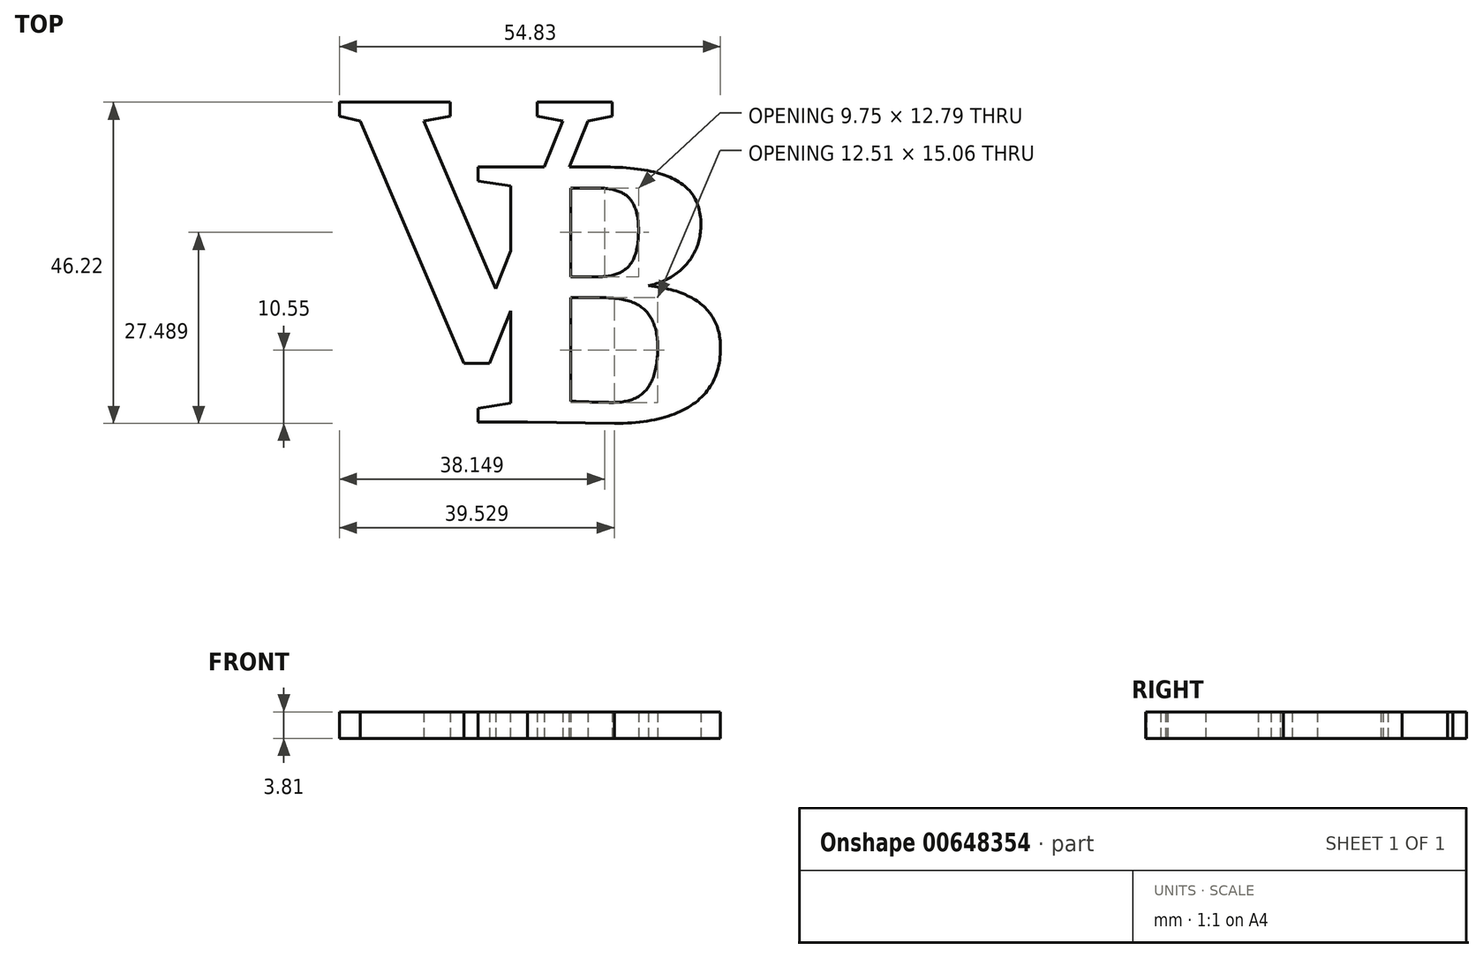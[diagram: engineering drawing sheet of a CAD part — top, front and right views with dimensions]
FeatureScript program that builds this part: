
annotation { "Feature Type Name" : "Feature", "Feature Type Description" : "" }
export const myFeature = defineFeature(function(context is Context, id is Id, definition is map)
    precondition{}
    {
        {
            var Q0;
            Q0=qCreatedBy(makeId("Top.planeOp"),FACE);
            var sketch = newSketch(context, id + "F0", { "sketchPlane" : qUnion([Q0])});
            skText(sketch, "E0", { "text": "V", "fontName": "Tinos-Bold.ttf"});
            const initialGuessF0  = {"E0": [-0.02997, -0.0202, 1, 0, 0.04038]};
            skSetInitialGuess(sketch, initialGuessF0);
            skSolve(sketch);
        }
        {
            var Q0;
            Q0 = qSketchRegion(id + "F0", true);
            extrude(context, id + "F1", {"entities" : qUnion([Q0]), "depth" : 3.8 * mm, "offsetDistance" : 25.4 * mm});
        }
        {
            var Q0;
            Q0=qCreatedBy(makeId("Top.planeOp"),FACE);
            var sketch = newSketch(context, id + "F2", { "sketchPlane" : qUnion([Q0])});
            skText(sketch, "E1", { "text": "B", "fontName": "Tinos-Bold.ttf"});
            const initialGuessF2  = {"E1": [-0.01036, -0.02952, 1, 0, 0.04038]};
            skSetInitialGuess(sketch, initialGuessF2);
            skSolve(sketch);
        }
        {
            var Q0;
            Q0 = qSketchRegion(id + "F2", true);
            extrude(context, id + "F3", {"entities" : qUnion([Q0]), "operationType" : NewBodyOperationType.ADD, "depth" : 3.8 * mm, "offsetDistance" : 25.4 * mm});
        }
    });
